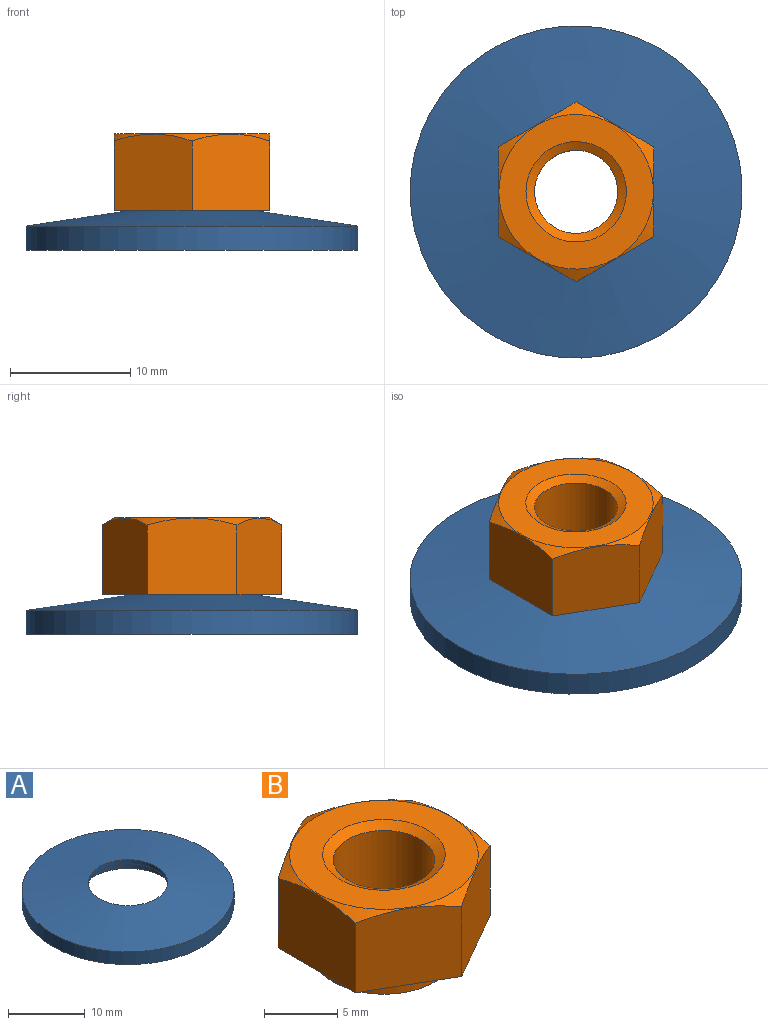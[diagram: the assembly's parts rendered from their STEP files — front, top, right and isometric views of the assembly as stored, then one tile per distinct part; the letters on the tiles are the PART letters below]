
ASSEMBLY  parts=2 mates=1
PART A: 6 faces, bbox 27.6x27.6x3.3 mm
  f0: cylinder r=6.31mm len=12.63mm, axis (0,0,-1), area 55.4mm2, adj f1,f5
  f1: cone r=6.31mm half-angle=81.6deg, axis (0,0,-1), area 479.3mm2, adj f0,f2
  f2: cylinder r=13.81mm len=27.63mm, axis (0,0,-1), area 175.5mm2, adj f1,f3
  f3: cone r=13.81mm half-angle=81.6deg, axis (0,0,-1), area 520.8mm2, adj f2,f4
  f4: cylinder r=5.17mm len=10.35mm, axis (0,0,-1), area 20.3mm2, adj f3,f5
  f5: cone r=5.17mm half-angle=81.6deg, axis (0,0,-1), area 41.5mm2, adj f0,f4
PART B: 15 faces, bbox 15x15x8.2 mm
  f0: cone r=6.43mm half-angle=60deg, axis (0,0,-1), area 17.6mm2, adj f1,f9,f10,f11,f12,f13,f14
  f1: plane 12.86x12.86mm, normal (0,0,1), area 75.2mm2, adj f0,f2
  f2: cone r=4.17mm half-angle=60deg, axis (0,0,1), area 19.9mm2, adj f1,f3
  f3: cylinder r=3.46mm len=6.91mm, axis (0,0,-1), area 122.2mm2, adj f2,f4
  f4: cone r=3.46mm half-angle=60deg, axis (0,0,-1), area 16.9mm2, adj f3,f5
  f5: cylinder r=4.07mm len=8.15mm, axis (0,0,-1), area 45.4mm2, adj f4,f6
  f6: plane 9.75x9.75mm, normal (0,0,-1), area 22.5mm2, adj f5,f7
  f7: cylinder r=4.88mm len=9.75mm, axis (0,0,-1), area 54.4mm2, adj f6,f8
  f8: plane 14.95x12.95mm, normal (0,0,-1), area 70.5mm2, adj f7,f9,f10,f11,f12,f13,f14
  f9: plane 6.47x6.38mm, normal (-0.5,-0.87,0), area 46.2mm2, adj f0,f8,f12,f13
  f10: plane 6.47x6.38mm, normal (-0.5,0.87,0), area 46.2mm2, adj f0,f8,f12,f14
  f11: plane 7.48x6.38mm, normal (1,0,0), area 46.2mm2, adj f0,f8,f13,f14
  f12: plane 7.48x6.38mm, normal (-1,0,0), area 46.2mm2, adj f0,f8,f9,f10
  f13: plane 6.47x6.38mm, normal (0.5,-0.87,0), area 46.2mm2, adj f0,f8,f9,f11
  f14: plane 6.47x6.38mm, normal (0.5,0.87,0), area 46.2mm2, adj f0,f8,f10,f11
PLACE A t=(0.19,-0.08,-15.84)mm
PLACE B t=(0.19,-0.08,-4.48)mm
MATE fastened B.f0 <-> A.f0  axis (0,0,-1) through (0.19,-0.08,1.36)mm
